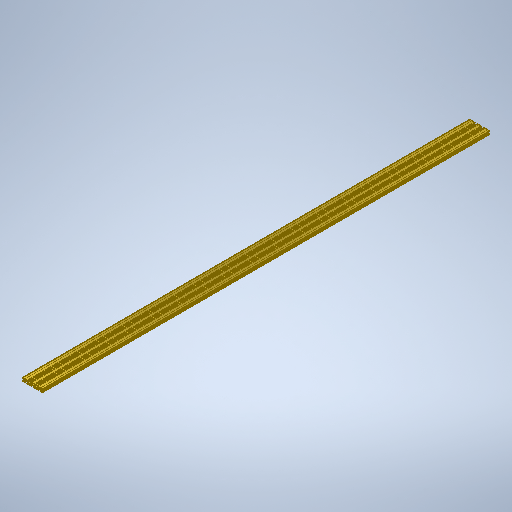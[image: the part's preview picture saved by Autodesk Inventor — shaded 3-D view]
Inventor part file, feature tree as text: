
AUTODESK INVENTOR PART (.ipt)
format: ipt  version: 2025.2 (Build 292293000, 293)  size: 536,064 bytes
history: native  units: mm
features: other x1, extrude x1, mirror x1, sketch x1
ambient origin geometry x8: Origin, YZ Plane, XZ Plane, XY Plane, X Axis, Y Axis, Z Axis, Center Point
bodies: Body1 (feature_tree)
feature tree (4):
  other  "Sólido1"
  extrude  "Extrusão1"  Depth=15.0mm
  mirror  "Espelhar1"
  sketch  "Esboço1"  dims[d0=90.0mm d5=15.0mm d6=5.5mm d7=6.2mm d9=1.5mm d10=3.0mm d24=0.5mm d74=8.2mm d75=30.0mm d76=15.0mm d79=2.2mm d81=2.2mm d86=0.5mm d87=2.2mm d88=2.2mm d90=2000.0mm d91=0.0mm d93=2.2mm]
